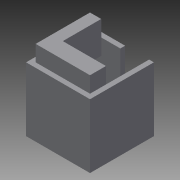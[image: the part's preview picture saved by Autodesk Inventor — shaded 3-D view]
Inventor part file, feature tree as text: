
AUTODESK INVENTOR PART (.ipt)
format: ipt  version: 2013 (Build 170138000, 138)  size: 101,376 bytes
history: native  units: mm
features: extrude x3, sketch x3, other x1
ambient origin geometry x8: Origin, YZ Plane, XZ Plane, XY Plane, X Axis, Y Axis, Z Axis, Center Point
feature tree (7):
  other  "ソリッド1"
  extrude  "押し出し1"  Depth=34.0mm
  extrude  "押し出し2"  Depth=34.0mm
  extrude  "押し出し3"  Depth=40.0mm
  sketch  "スケッチ1"
  sketch  "スケッチ2"
  sketch  "スケッチ3"
